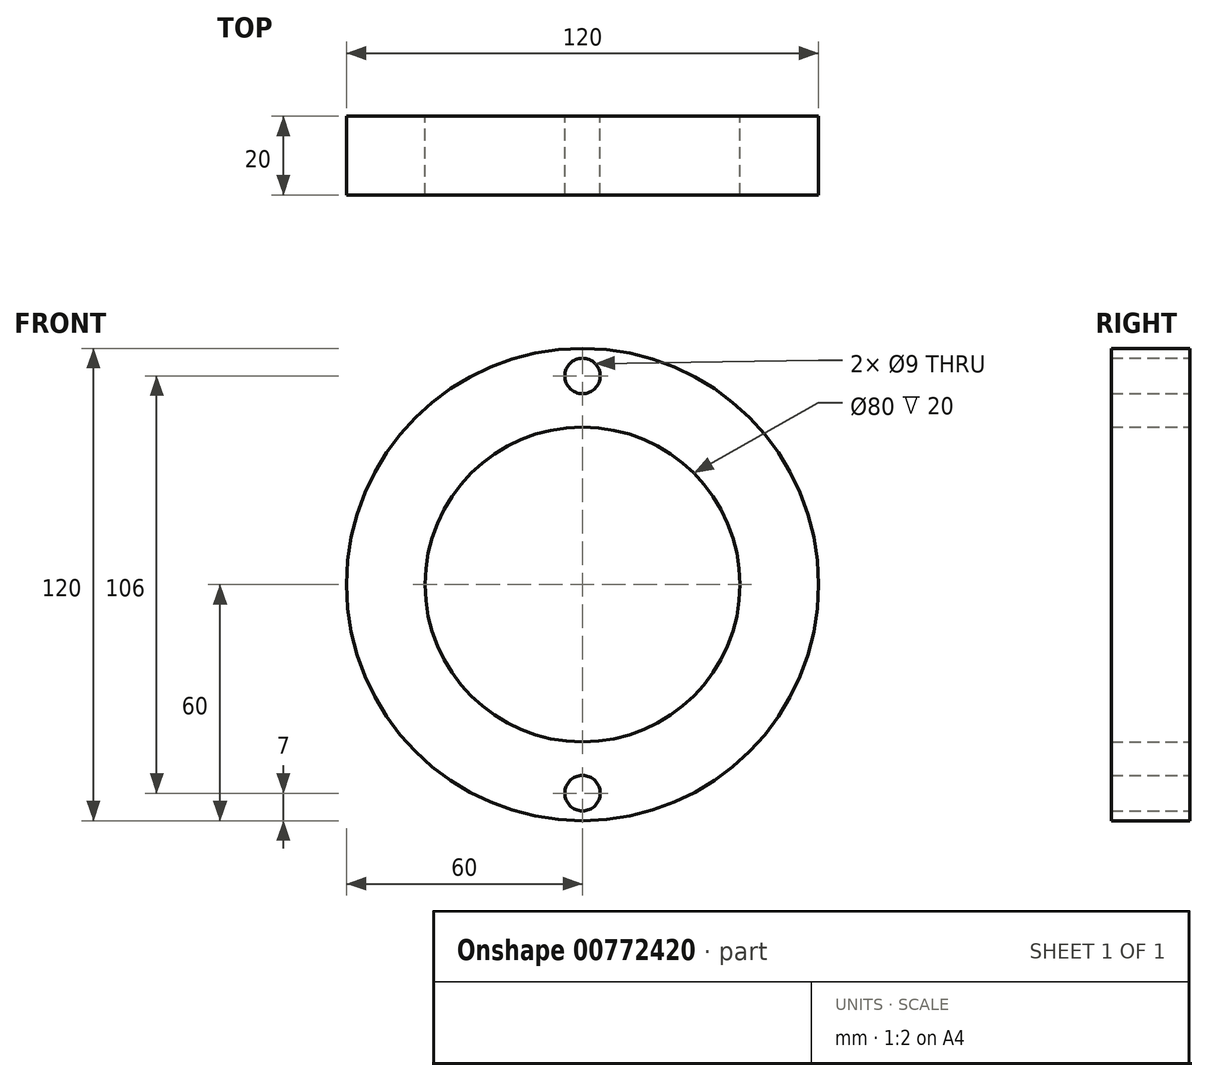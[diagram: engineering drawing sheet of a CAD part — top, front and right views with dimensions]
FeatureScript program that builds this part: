
annotation { "Feature Type Name" : "Feature", "Feature Type Description" : "" }
export const myFeature = defineFeature(function(context is Context, id is Id, definition is map)
    precondition{}
    {
        {
            var Q0;
            Q0=qCreatedBy(makeId("Front.planeOp"),FACE);
            var sketch = newSketch(context, id + "F0", { "sketchPlane" : qUnion([Q0])});
            skCircle(sketch, "E0", {"center": v(0, 0) * mm, "radius": 60 * mm});
            skCircle(sketch, "E1", {"center": v(0, 0) * mm, "radius": 40 * mm});
            skCircle(sketch, "E2", {"center": v(0, 53) * mm, "radius": 4.5 * mm});
            skCircle(sketch, "E3", {"center": v(0, -53) * mm, "radius": 4.5 * mm});
            skSolve(sketch);
        }
        {
            var Q0;
            Q0=makeQuery(id+"F0.imprint","IMPRINT",FACE,{"disambiguationData":[TD([[makeQuery(id+"F0.imprint","IMPRINT",EDGE,{"derivedFrom":sQuery(id+"F0.wireOp",EDGE,"E0")}),1.0]])]});
            extrude(context, id + "F1", {"entities" : qUnion([Q0]), "depth" : 20 * mm, "offsetDistance" : 25.4 * mm});
        }
    });
